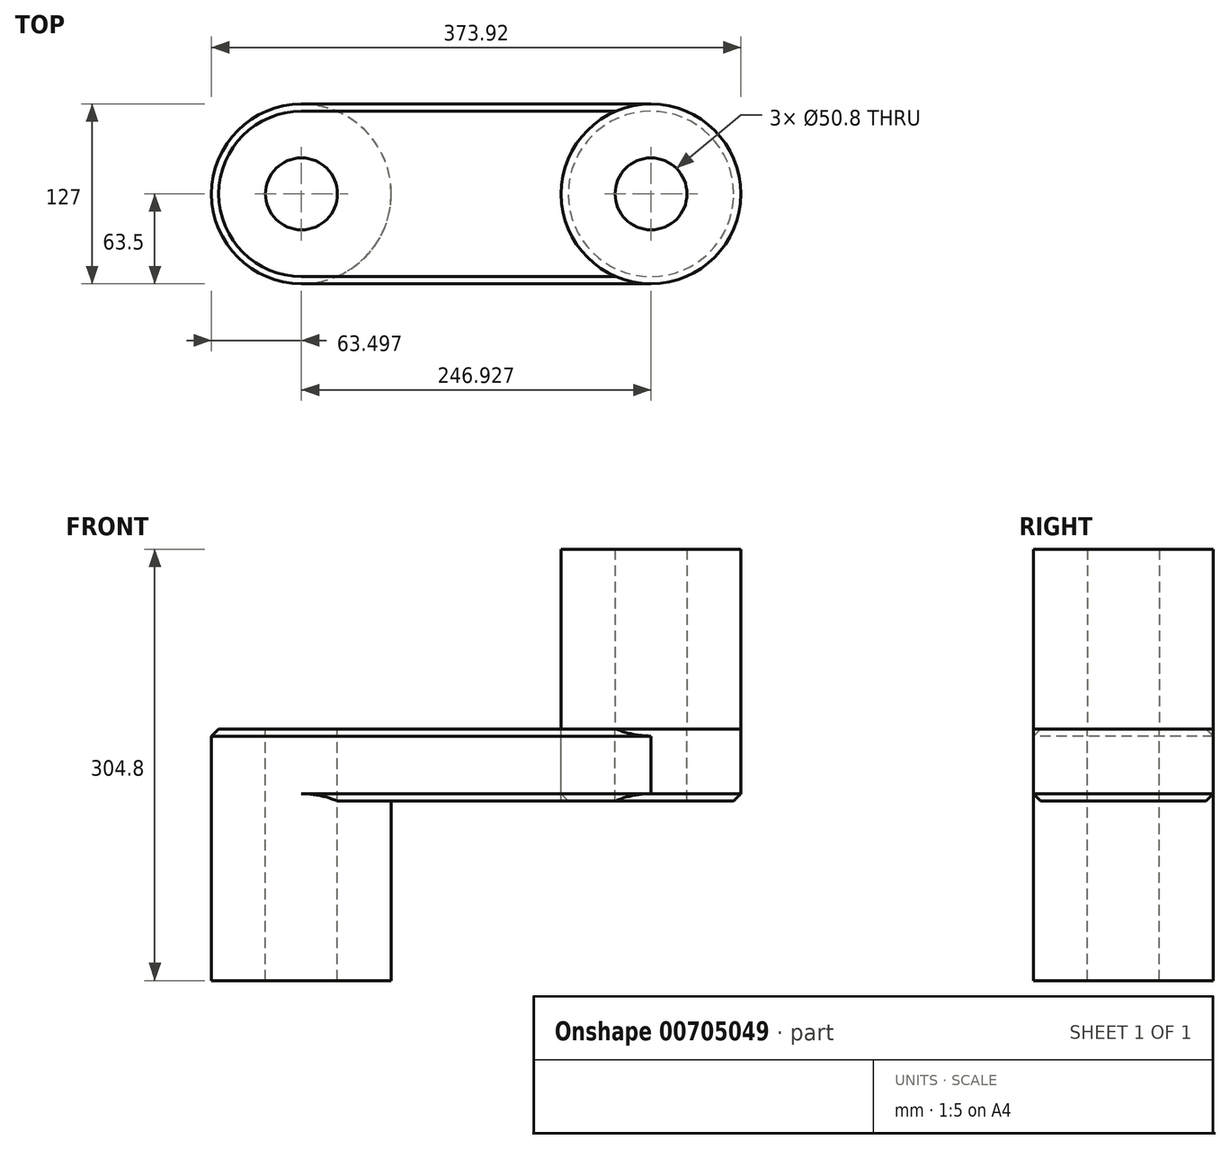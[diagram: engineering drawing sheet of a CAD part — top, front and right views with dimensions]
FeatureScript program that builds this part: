
annotation { "Feature Type Name" : "Feature", "Feature Type Description" : "" }
export const myFeature = defineFeature(function(context is Context, id is Id, definition is map)
    precondition{}
    {
        {
            var Q0;
            Q0=qCreatedBy(makeId("Top.planeOp"),FACE);
            var sketch = newSketch(context, id + "F0", { "sketchPlane" : qUnion([Q0])});
            skLineSegment(sketch, "E0.bottom", {"start": v(123.46, -63.5) * mm, "end": v(-123.46, -63.5) * mm});
            skLineSegment(sketch, "E0.top", {"start": v(123.46, 63.5) * mm, "end": v(-123.46, 63.5) * mm});
            skLineSegment(sketch, "E0.left", {"start": v(123.46, -63.5) * mm, "end": v(123.46, 63.5) * mm});
            skLineSegment(sketch, "E0.right", {"start": v(-123.46, -63.5) * mm, "end": v(-123.46, 63.5) * mm});
            skPoint(sketch, "E0.middle", {"position": v(0, 0) * mm});
            skCircle(sketch, "E1", {"center": v(-123.46, 0) * mm, "radius": 63.5 * mm});
            skCircle(sketch, "E2", {"center": v(123.46, 0) * mm, "radius": 63.5 * mm});
            skCircle(sketch, "E3", {"center": v(-123.46, 0) * mm, "radius": 25.4 * mm});
            skCircle(sketch, "E4", {"center": v(123.46, 0) * mm, "radius": 25.4 * mm});
            skSolve(sketch);
        }
        {
            var Q0;
            {var subQ1=sQuery(id+"F0.wireOp",EDGE,"E0.left");var subQ3=sQuery(id+"F0.wireOp",EDGE,"E4");var subQ4=makeQuery(id+"F0.imprint","INTERSECT",VERTEX,{"disambiguationData":[OD(0.0)],"derivedFrom":[subQ1,subQ3]});Q0=makeQuery(id+"F0.imprint","IMPRINT",FACE,{"disambiguationData":[TD([[makeQuery(id+"F0.imprint","IMPRINT",EDGE,{"disambiguationData":[TD([[subQ4,1.0]])],"derivedFrom":subQ3}),-1.0]])]});}
            var Q1;
            {var subQ1=sQuery(id+"F0.wireOp",EDGE,"E0.left");var subQ3=sQuery(id+"F0.wireOp",EDGE,"E4");var subQ4=makeQuery(id+"F0.imprint","INTERSECT",VERTEX,{"disambiguationData":[OD(0.0)],"derivedFrom":[subQ1,subQ3]});Q1=makeQuery(id+"F0.imprint","IMPRINT",FACE,{"disambiguationData":[TD([[makeQuery(id+"F0.imprint","IMPRINT",EDGE,{"disambiguationData":[TD([[subQ4,-1.0]])],"derivedFrom":subQ3}),-1.0]])]});}
            extrude(context, id + "F1", {"entities" : qUnion([Q0, Q1]), "depth" : 127 * mm, "offsetDistance" : 25.4 * mm});
        }
        {
            var Q0;
            {var subQ1=sQuery(id+"F0.wireOp",EDGE,"E0.right");var subQ3=sQuery(id+"F0.wireOp",EDGE,"E3");var subQ4=makeQuery(id+"F0.imprint","INTERSECT",VERTEX,{"disambiguationData":[OD(0.0)],"derivedFrom":[subQ1,subQ3]});Q0=makeQuery(id+"F0.imprint","IMPRINT",FACE,{"disambiguationData":[TD([[makeQuery(id+"F0.imprint","IMPRINT",EDGE,{"disambiguationData":[TD([[subQ4,1.0]])],"derivedFrom":subQ3}),-1.0]])]});}
            var Q1;
            {var subQ1=sQuery(id+"F0.wireOp",EDGE,"E0.right");var subQ3=sQuery(id+"F0.wireOp",EDGE,"E3");var subQ4=makeQuery(id+"F0.imprint","INTERSECT",VERTEX,{"disambiguationData":[OD(0.0)],"derivedFrom":[subQ1,subQ3]});Q1=makeQuery(id+"F0.imprint","IMPRINT",FACE,{"disambiguationData":[TD([[makeQuery(id+"F0.imprint","IMPRINT",EDGE,{"disambiguationData":[TD([[subQ4,-1.0]])],"derivedFrom":subQ3}),-1.0]])]});}
            extrude(context, id + "F2", {"entities" : qUnion([Q0, Q1]), "oppositeDirection" : true, "depth" : 177.8 * mm, "offsetDistance" : 25.4 * mm});
        }
        {
            var Q0;
            {var subQ0=sQuery(id+"F0.wireOp",EDGE,"E0.bottom");Q0=makeQuery(id+"F0.imprint","IMPRINT",FACE,{"disambiguationData":[TD([[makeQuery(id+"F0.imprint","IMPRINT",EDGE,{"derivedFrom":subQ0}),-1.0]])]});}
            extrude(context, id + "F3", {"entities" : qUnion([Q0]), "operationType" : NewBodyOperationType.ADD, "oppositeDirection" : true, "depth" : 50.8 * mm, "offsetDistance" : 25.4 * mm});
        }
        {
            var Q0;
            {var subQ1=sQuery(id+"F0.wireOp",EDGE,"E0.left");var subQ3=sQuery(id+"F0.wireOp",EDGE,"E4");var subQ4=makeQuery(id+"F0.imprint","INTERSECT",VERTEX,{"disambiguationData":[OD(0.0)],"derivedFrom":[subQ1,subQ3]});Q0=makeQuery(id+"F0.imprint","IMPRINT",FACE,{"disambiguationData":[TD([[makeQuery(id+"F0.imprint","IMPRINT",EDGE,{"disambiguationData":[TD([[subQ4,-1.0]])],"derivedFrom":subQ3}),-1.0]])]});}
            var Q1;
            {var subQ1=sQuery(id+"F0.wireOp",EDGE,"E0.left");var subQ3=sQuery(id+"F0.wireOp",EDGE,"E4");var subQ4=makeQuery(id+"F0.imprint","INTERSECT",VERTEX,{"disambiguationData":[OD(0.0)],"derivedFrom":[subQ1,subQ3]});Q1=makeQuery(id+"F0.imprint","IMPRINT",FACE,{"disambiguationData":[TD([[makeQuery(id+"F0.imprint","IMPRINT",EDGE,{"disambiguationData":[TD([[subQ4,1.0]])],"derivedFrom":subQ3}),-1.0]])]});}
            extrude(context, id + "F4", {"entities" : qUnion([Q0, Q1]), "oppositeDirection" : true, "depth" : 50.8 * mm, "offsetDistance" : 25.4 * mm});
        }
        {
            var Q0;
            Q0=makeQuery(id+"F2.opExtrude","CAP_EDGE",EDGE,{"disambiguationData":[OSD([sQuery(id+"F0.wireOp",EDGE,"E1")])],"isStart":true});
            var Q1;
            Q1=makeQuery(id+"F3.opExtrude","CAP_EDGE",EDGE,{"disambiguationData":[OSD([sQuery(id+"F0.wireOp",EDGE,"E0.bottom")])],"isStart":false});
            var Q2;
            Q2=makeQuery(id+"F4.opExtrude","CAP_EDGE",EDGE,{"disambiguationData":[OSD([sQuery(id+"F0.wireOp",EDGE,"E2")])],"isStart":false});
            var Q3;
            Q3=makeQuery(id+"F3.opExtrude","CAP_EDGE",EDGE,{"disambiguationData":[OSD([sQuery(id+"F0.wireOp",EDGE,"E0.top")])],"isStart":false});
            chamfer(context, id + "F5", {"entities" : qUnion([Q0, Q1, Q2, Q3]), "width" : 5.08 * mm, "tangentPropagation" : true});
        }
    });
